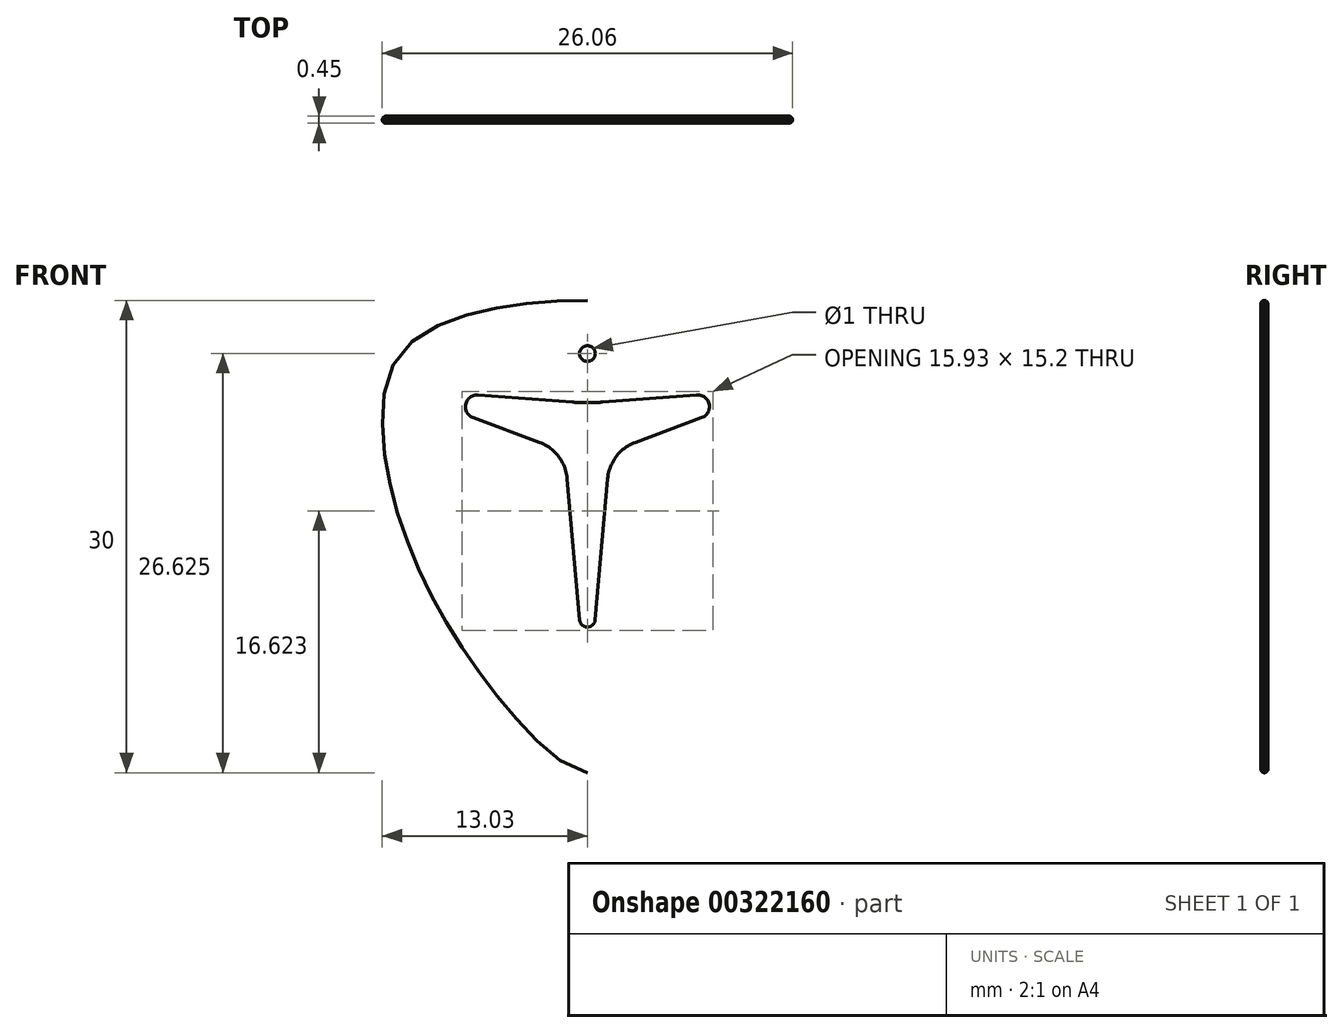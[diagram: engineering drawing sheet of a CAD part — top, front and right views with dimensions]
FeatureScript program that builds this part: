
annotation { "Feature Type Name" : "Feature", "Feature Type Description" : "" }
export const myFeature = defineFeature(function(context is Context, id is Id, definition is map)
    precondition{}
    {
        {
            var Q0;
            Q0=qCreatedBy(makeId("Front.planeOp"),FACE);
            var sketch = newSketch(context, id + "F0", { "sketchPlane" : qUnion([Q0])});
            skLineSegment(sketch, "E0", {"start": v(0, 0) * mm, "end": v(0, 6.75) * mm, "construction": true});
            skLineSegment(sketch, "E1", {"start": v(0, 0) * mm, "end": v(0, -23.25) * mm, "construction": true});
            skLineSegment(sketch, "E2", {"start": v(0, 0) * mm, "end": v(13, 0) * mm, "construction": true});
            skFitSpline(sketch, "E3", {"points": [v(0, -23.25) * mm, v(9.5, -12.75) * mm, v(13, 0) * mm, v(11, 4.25) * mm, v(0, 6.75) * mm], "startDerivative": vector(20.6, 0) * mm, "endDerivative": vector(-57.72, 0) * mm});
            skFitSpline(sketch, "E4.MirrorCS", {"points": [v(0, -23.25) * mm, v(-9.5, -12.75) * mm, v(-13, 0) * mm, v(-11, 4.25) * mm, v(0, 6.75) * mm], "startDerivative": vector(-20.6, 0) * mm, "endDerivative": vector(57.72, 0) * mm});
            skArc(sketch, "E5", {"start": v(7.26, -0.7) * mm, "mid": v(7.73, 0.16) * mm, "end": v(6.94, 0.75) * mm});
            skLineSegment(sketch, "E6", {"start": v(7.26, -0.7) * mm, "end": v(3.04, -2.27) * mm});
            skArc(sketch, "E7", {"start": v(3.04, -2.27) * mm, "mid": v(1.83, -3.17) * mm, "end": v(1.28, -4.58) * mm});
            skLineSegment(sketch, "E8", {"start": v(0.5, -13.54) * mm, "end": v(1.28, -4.58) * mm});
            skArc(sketch, "E9", {"start": v(0, -14) * mm, "mid": v(0.34, -13.87) * mm, "end": v(0.5, -13.54) * mm});
            skArc(sketch, "E10.MirrorCS", {"start": v(0, -14) * mm, "mid": v(-0.34, -13.87) * mm, "end": v(-0.5, -13.54) * mm});
            skLineSegment(sketch, "E11.MirrorCS", {"start": v(-0.5, -13.54) * mm, "end": v(-1.28, -4.58) * mm});
            skArc(sketch, "E12.MirrorCS", {"start": v(-3.04, -2.27) * mm, "mid": v(-1.83, -3.17) * mm, "end": v(-1.28, -4.58) * mm});
            skLineSegment(sketch, "E13.MirrorCS", {"start": v(-7.26, -0.7) * mm, "end": v(-3.04, -2.27) * mm});
            skArc(sketch, "E14.MirrorCS", {"start": v(-7.26, -0.7) * mm, "mid": v(-7.73, 0.16) * mm, "end": v(-6.94, 0.75) * mm});
            skLineSegment(sketch, "E15", {"start": v(6.94, 0.75) * mm, "end": v(0.96, 0.29) * mm});
            skArc(sketch, "E16", {"start": v(0, 0.25) * mm, "mid": v(0.48, 0.26) * mm, "end": v(0.96, 0.29) * mm});
            skArc(sketch, "E17.MirrorCS", {"start": v(0, 0.25) * mm, "mid": v(-0.48, 0.26) * mm, "end": v(-0.96, 0.29) * mm});
            skLineSegment(sketch, "E18.MirrorCS", {"start": v(-6.94, 0.75) * mm, "end": v(-0.96, 0.29) * mm});
            skCircle(sketch, "E19", {"center": v(0, 3.38) * mm, "radius": 0.5 * mm});
            skSolve(sketch);
        }
        {
            var Q0;
            Q0=qSketchRegion(id+"F0",true);
            extrude(context, id + "F1", {"entities" : qUnion([Q0]), "depth" : 0.45 * mm});
        }
        {
            var Q0;
            Q0=makeQuery(id+"F1.opExtrude","CAP_EDGE",EDGE,{"disambiguationData":[OSD([sQuery(id+"F0.wireOp",EDGE,"E5")])],"isStart":false});
            var Q1;
            Q1=makeQuery(id+"F1.opExtrude","CAP_EDGE",EDGE,{"disambiguationData":[OSD([sQuery(id+"F0.wireOp",EDGE,"E7")])],"isStart":true});
            var Q2;
            Q2=makeQuery(id+"F1.opExtrude","CAP_EDGE",EDGE,{"disambiguationData":[OSD([sQuery(id+"F0.wireOp",EDGE,"E9"),sQuery(id+"F0.wireOp",EDGE,"E10.MirrorCS")])],"isStart":false});
            var Q3;
            Q3=makeQuery(id+"F1.opExtrude","CAP_EDGE",EDGE,{"disambiguationData":[OSD([sQuery(id+"F0.wireOp",EDGE,"E14.MirrorCS")])],"isStart":false});
            var Q4;
            Q4=makeQuery(id+"F1.opExtrude","CAP_EDGE",EDGE,{"disambiguationData":[OSD([sQuery(id+"F0.wireOp",EDGE,"E5")])],"isStart":true});
            var Q5;
            Q5=makeQuery(id+"F1.opExtrude","CAP_EDGE",EDGE,{"disambiguationData":[OSD([sQuery(id+"F0.wireOp",EDGE,"E12.MirrorCS")])],"isStart":false});
            var Q6;
            Q6=makeQuery(id+"F1.opExtrude","CAP_EDGE",EDGE,{"disambiguationData":[OSD([sQuery(id+"F0.wireOp",EDGE,"E7")])],"isStart":false});
            var Q7;
            Q7=makeQuery(id+"F1.opExtrude","CAP_EDGE",EDGE,{"disambiguationData":[OSD([sQuery(id+"F0.wireOp",EDGE,"cP70XH3B-hxny-nh1n-TbyW-52Zl4TOD4HrO"),sQuery(id+"F0.wireOp",EDGE,"9cf6c757-e815-40dd-95a7-672993b90d513.MirrorCS")])],"isStart":true});
            var Q8;
            Q8=makeQuery(id+"F1.opExtrude","CAP_EDGE",EDGE,{"disambiguationData":[OSD([sQuery(id+"F0.wireOp",EDGE,"E13.MirrorCS")])],"isStart":false});
            var Q9;
            Q9=makeQuery(id+"F1.opExtrude","CAP_EDGE",EDGE,{"disambiguationData":[OSD([sQuery(id+"F0.wireOp",EDGE,"E12.MirrorCS")])],"isStart":true});
            var Q10;
            Q10=makeQuery(id+"F1.opExtrude","CAP_EDGE",EDGE,{"disambiguationData":[OSD([sQuery(id+"F0.wireOp",EDGE,"cP70XH3B-hxny-nh1n-TbyW-52Zl4TOD4HrO"),sQuery(id+"F0.wireOp",EDGE,"9cf6c757-e815-40dd-95a7-672993b90d513.MirrorCS")])],"isStart":false});
            var Q11;
            Q11=makeQuery(id+"F1.opExtrude","CAP_EDGE",EDGE,{"disambiguationData":[OSD([sQuery(id+"F0.wireOp",EDGE,"E9"),sQuery(id+"F0.wireOp",EDGE,"E10.MirrorCS")])],"isStart":true});
            var Q12;
            Q12=makeQuery(id+"F1.opExtrude","SWEPT_EDGE",EDGE,{"disambiguationData":[OSD([sQuery(id+"F0.wireOp",EDGE,"9cf6c757-e815-40dd-95a7-672993b90d513.MirrorCS"),sQuery(id+"F0.wireOp",EDGE,"E14.MirrorCS")])]});
            var Q13;
            Q13=makeQuery(id+"F1.opExtrude","CAP_EDGE",EDGE,{"disambiguationData":[OSD([sQuery(id+"F0.wireOp",EDGE,"E8")])],"isStart":true});
            var Q14;
            Q14=makeQuery(id+"F1.opExtrude","CAP_EDGE",EDGE,{"disambiguationData":[OSD([sQuery(id+"F0.wireOp",EDGE,"E11.MirrorCS")])],"isStart":false});
            var Q15;
            Q15=makeQuery(id+"F1.opExtrude","SWEPT_EDGE",EDGE,{"disambiguationData":[OSD([sQuery(id+"F0.wireOp",EDGE,"E6"),sQuery(id+"F0.wireOp",EDGE,"E7")])]});
            var Q16;
            Q16=makeQuery(id+"F1.opExtrude","SWEPT_EDGE",EDGE,{"disambiguationData":[OSD([sQuery(id+"F0.wireOp",EDGE,"E8"),sQuery(id+"F0.wireOp",EDGE,"E9")])]});
            var Q17;
            Q17=makeQuery(id+"F1.opExtrude","SWEPT_EDGE",EDGE,{"disambiguationData":[OSD([sQuery(id+"F0.wireOp",EDGE,"E13.MirrorCS"),sQuery(id+"F0.wireOp",EDGE,"E14.MirrorCS")])]});
            var Q18;
            Q18=makeQuery(id+"F1.opExtrude","SWEPT_EDGE",EDGE,{"disambiguationData":[OSD([sQuery(id+"F0.wireOp",EDGE,"E10.MirrorCS"),sQuery(id+"F0.wireOp",EDGE,"E11.MirrorCS")])]});
            var Q19;
            Q19=makeQuery(id+"F1.opExtrude","SWEPT_EDGE",EDGE,{"disambiguationData":[OSD([sQuery(id+"F0.wireOp",EDGE,"E11.MirrorCS"),sQuery(id+"F0.wireOp",EDGE,"E12.MirrorCS")])]});
            var Q20;
            Q20=makeQuery(id+"F1.opExtrude","SWEPT_EDGE",EDGE,{"disambiguationData":[OSD([sQuery(id+"F0.wireOp",EDGE,"E5"),sQuery(id+"F0.wireOp",EDGE,"E6")])]});
            var Q21;
            Q21=makeQuery(id+"F1.opExtrude","CAP_EDGE",EDGE,{"disambiguationData":[OSD([sQuery(id+"F0.wireOp",EDGE,"E14.MirrorCS")])],"isStart":true});
            var Q22;
            Q22=makeQuery(id+"F1.opExtrude","SWEPT_EDGE",EDGE,{"disambiguationData":[OSD([sQuery(id+"F0.wireOp",EDGE,"E12.MirrorCS"),sQuery(id+"F0.wireOp",EDGE,"E13.MirrorCS")])]});
            var Q23;
            Q23=makeQuery(id+"F1.opExtrude","CAP_EDGE",EDGE,{"disambiguationData":[OSD([sQuery(id+"F0.wireOp",EDGE,"E8")])],"isStart":false});
            var Q24;
            Q24=makeQuery(id+"F1.opExtrude","SWEPT_EDGE",EDGE,{"disambiguationData":[OSD([sQuery(id+"F0.wireOp",EDGE,"cP70XH3B-hxny-nh1n-TbyW-52Zl4TOD4HrO"),sQuery(id+"F0.wireOp",EDGE,"E5")])]});
            var Q25;
            Q25=makeQuery(id+"F1.opExtrude","CAP_EDGE",EDGE,{"disambiguationData":[OSD([sQuery(id+"F0.wireOp",EDGE,"E6")])],"isStart":false});
            var Q26;
            Q26=makeQuery(id+"F1.opExtrude","CAP_EDGE",EDGE,{"disambiguationData":[OSD([sQuery(id+"F0.wireOp",EDGE,"E11.MirrorCS")])],"isStart":true});
            var Q27;
            Q27=makeQuery(id+"F1.opExtrude","SWEPT_EDGE",EDGE,{"disambiguationData":[OSD([sQuery(id+"F0.wireOp",EDGE,"E7"),sQuery(id+"F0.wireOp",EDGE,"E8")])]});
            var Q28;
            Q28=makeQuery(id+"F1.opExtrude","CAP_EDGE",EDGE,{"disambiguationData":[OSD([sQuery(id+"F0.wireOp",EDGE,"E6")])],"isStart":true});
            var Q29;
            Q29=makeQuery(id+"F1.opExtrude","CAP_EDGE",EDGE,{"disambiguationData":[OSD([sQuery(id+"F0.wireOp",EDGE,"E13.MirrorCS")])],"isStart":true});
            var Q30;
            Q30=makeQuery(id+"F1.opExtrude","CAP_EDGE",EDGE,{"disambiguationData":[OSD([sQuery(id+"F0.wireOp",EDGE,"E18.MirrorCS")])],"isStart":false});
            var Q31;
            Q31=makeQuery(id+"F1.opExtrude","CAP_EDGE",EDGE,{"disambiguationData":[OSD([sQuery(id+"F0.wireOp",EDGE,"E18.MirrorCS")])],"isStart":true});
            var Q32;
            Q32=makeQuery(id+"F1.opExtrude","CAP_EDGE",EDGE,{"disambiguationData":[OSD([sQuery(id+"F0.wireOp",EDGE,"E16"),sQuery(id+"F0.wireOp",EDGE,"E17.MirrorCS")])],"isStart":false});
            var Q33;
            Q33=makeQuery(id+"F1.opExtrude","CAP_EDGE",EDGE,{"disambiguationData":[OSD([sQuery(id+"F0.wireOp",EDGE,"E16"),sQuery(id+"F0.wireOp",EDGE,"E17.MirrorCS")])],"isStart":true});
            var Q34;
            Q34=makeQuery(id+"F1.opExtrude","CAP_EDGE",EDGE,{"disambiguationData":[OSD([sQuery(id+"F0.wireOp",EDGE,"E15")])],"isStart":false});
            fillet(context, id + "F2", {"entities" : qUnion([Q0, Q1, Q2, Q3, Q4, Q5, Q6, Q7, Q8, Q9, Q10, Q11, Q12, Q13, Q14, Q15, Q16, Q17, Q18, Q19, Q20, Q21, Q22, Q23, Q24, Q25, Q26, Q27, Q28, Q29, Q30, Q31, Q32, Q33, Q34]), "radius" : (0.45 / 2) * mm, "tangentPropagation" : true, "allowEdgeOverflow" : false});
        }
        {
            var Q0;
            Q0=makeQuery(id+"F1.opExtrude","CAP_EDGE",EDGE,{"disambiguationData":[OSD([sQuery(id+"F0.wireOp",EDGE,"E4.MirrorCS")])],"isStart":false});
            var Q1;
            Q1=makeQuery(id+"F1.opExtrude","CAP_EDGE",EDGE,{"disambiguationData":[OSD([sQuery(id+"F0.wireOp",EDGE,"E3")])],"isStart":false});
            var Q2;
            Q2=makeQuery(id+"F1.opExtrude","CAP_EDGE",EDGE,{"disambiguationData":[OSD([sQuery(id+"F0.wireOp",EDGE,"E4.MirrorCS")])],"isStart":true});
            var Q3;
            Q3=makeQuery(id+"F1.opExtrude","CAP_EDGE",EDGE,{"disambiguationData":[OSD([sQuery(id+"F0.wireOp",EDGE,"E3")])],"isStart":true});
            fillet(context, id + "F3", {"entities" : qUnion([Q0, Q1, Q2, Q3]), "radius" : 0.45 / 2 * mm, "tangentPropagation" : true, "allowEdgeOverflow" : false});
        }
    });
